# Revit family: 17161 Скамейка стальная «Филигран Радиус» без спинки Хоббика
name_source: partatom
category: Антураж
revit_build: Autodesk Revit 2018 (Build: 20180423_1000(x64)
units: mm (PartAtom-declared; Revit-internal decimal feet)

## family parameters
Всегда вертикально = Да
Источник визуального образа = Геометрия семейства
На основе рабочей плоскости = Нет
Общий = Нет
При загрузке вырезать с полостями = Нет
Точка расчета площади = Нет

## types (1)
- Скамейка стальная «Филигран Радиус» без спинки 1 м.п.
    URL = https://hobbyka.ru
    θ = 35.81°
    Артикул товара = Арт. 17161
    Высота = 450 мм
    Группа модели = Скамейки
    Длина = 1000 мм
    Изготовитель = ООО «Хоббика»
    Изображение типоразмера = Скамейка стальная «Филигран Радиус» без спинки Арт 17161.jpg
    Материал изделия = Сталь, дерево
    Описание = Скамейка стальная «Филигран Радиус» без спинки. 1 м.п.
    Опора = 1200 мм
    Радиус = 1600 мм
    Радиус вн. = 1000 мм
    Радиус декора 1 = 1298 мм
    Радиус декора 2 = 1303 мм
    Цвет лавки = Дерево
    Цвет опоры = Сталь
    Ширина = 600 мм
